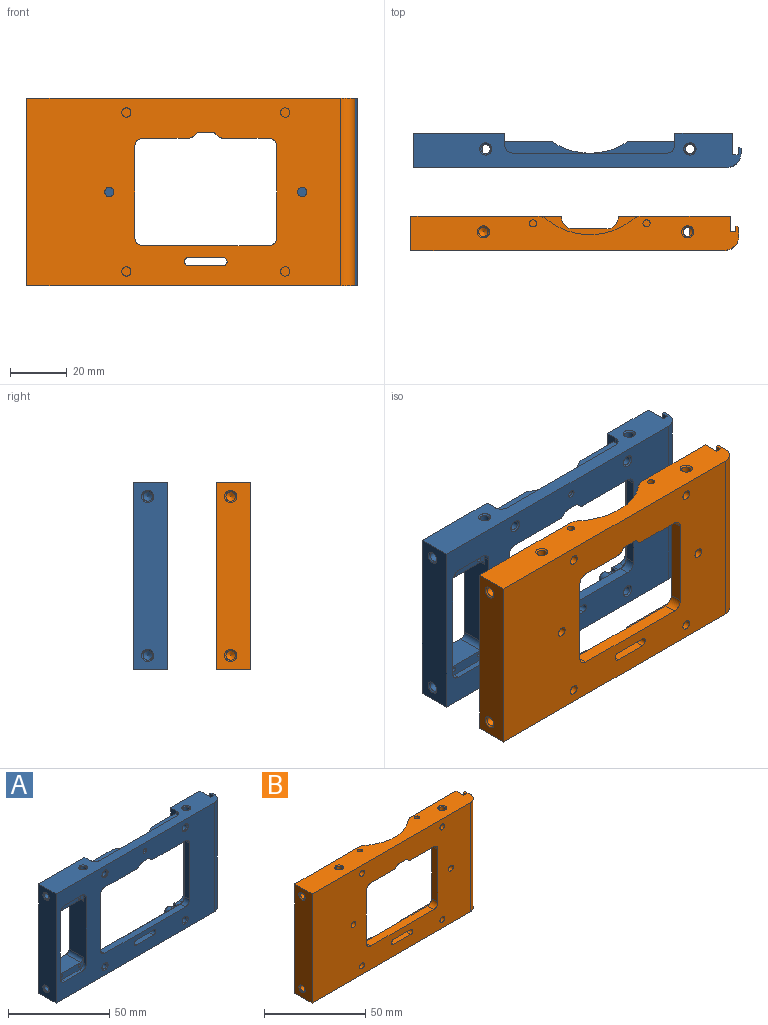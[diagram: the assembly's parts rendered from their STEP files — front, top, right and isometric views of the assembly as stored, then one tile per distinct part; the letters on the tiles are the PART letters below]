
ASSEMBLY  parts=2 mates=1
PART A: 193 faces, bbox 115.5x12x66 mm
  f0: plane 110.5x66mm, normal (0,-1,0), area 3867.2mm2, adj f15,f33,f34,f35,f36,f37,f38,f39
  f1: cylinder r=2mm len=10mm, axis (0,1,0), area 31.4mm2, adj f2,f31,f121,f173
  f2: plane 14.1x10mm, normal (0,0,-1), area 141mm2, adj f1,f3,f31,f173
  f3: cylinder r=2mm len=10mm, axis (0,1,0), area 31.4mm2, adj f2,f31,f122,f173
  f4: cylinder r=2mm len=10mm, axis (0,1,0), area 31.4mm2, adj f5,f31,f122,f177
  f5: plane 14.1x10mm, normal (0,0,1), area 141mm2, adj f4,f6,f31,f177
  f6: cylinder r=2mm len=10mm, axis (0,1,0), area 31.4mm2, adj f5,f31,f121,f177
  f7: cylinder r=0.8mm len=10mm, axis (0,-1,0), area 50.3mm2, adj f31,f173
  f8: cylinder r=0.8mm len=10mm, axis (0,-1,0), area 50.3mm2, adj f31,f177
  f9: cylinder r=0.8mm len=10mm, axis (0,-1,0), area 50.3mm2, adj f31,f177
  f10: cylinder r=0.8mm len=10mm, axis (0,-1,0), area 50.3mm2, adj f31,f173
  f11: plane 4.5x4.26mm, normal (1,0,0), area 19.2mm2, adj f15,f21,f139,f148
  f12: plane 4.5x4.26mm, normal (-1,0,0), area 19.2mm2, adj f15,f21,f140,f149
  f13: cylinder r=3.5mm len=4.5mm, axis (0,-1,0), area 6.6mm2, adj f21,f113,f139,f147
  f14: cylinder r=3.5mm len=4.5mm, axis (0,-1,0), area 6.6mm2, adj f18,f21,f140,f150
  f15: plane 115.5x12mm, normal (0,0,-1), area 923.5mm2, adj f0,f11,f12,f21,f24,f31,f54,f56
  f16: cylinder r=1.65mm len=8.5mm, axis (0,1,0), area 88.1mm2, adj f123,f140
  f17: cylinder r=1.65mm len=8.5mm, axis (0,1,0), area 88.1mm2, adj f126,f139
  f18: cylinder r=5mm len=7.5mm, axis (0,-1,0), area 16mm2, adj f14,f21,f24,f90,f119,f140
  f19: cylinder r=2mm len=4.5mm, axis (0,-1,0), area 26.3mm2, adj f21,f140,f149,f150
  f20: cylinder r=2mm len=4.5mm, axis (0,-1,0), area 26.3mm2, adj f21,f139,f147,f148
  f21: plane 78x56.5mm, normal (0,1,0), area 1353.3mm2, adj f11,f12,f13,f14,f15,f18,f19,f20
  f22: plane 8.11x7.5mm, normal (0,0,-1), area 48mm2, adj f21,f24,f49,f94,f116,f128,f138
  f23: plane 8.11x7.5mm, normal (0,0,-1), area 52.5mm2, adj f21,f31,f69,f93,f117,f127,f135
  f24: plane 66x20.3mm, normal (0,1,0), area 508.5mm2, adj f15,f18,f22,f55,f59,f86,f87,f90
  f25: cylinder r=24mm len=26.53mm, axis (0,0,1), area 208.8mm2, adj f28,f29,f30,f57,f127,f128
  f26: cylinder r=1.65mm len=8.5mm, axis (0,1,0), area 88.1mm2, adj f125,f127
  f27: cylinder r=1.65mm len=8.5mm, axis (0,1,0), area 88.1mm2, adj f124,f128
  f28: plane 43.29x4.5mm, normal (0,0,-1), area 122.8mm2, adj f21,f25,f127,f128,f136,f137
  f29: plane 30x4mm, normal (0,0,1), area 82.1mm2, adj f25,f114,f115,f116,f128
  f30: plane 30x4mm, normal (0,0,1), area 82.1mm2, adj f25,f114,f117,f118,f127
  f31: plane 66x32.2mm, normal (0,1,0), area 956.1mm2, adj f1,f2,f3,f4,f5,f6,f7,f8
  f32: plane 7.5x3.18mm, normal (0,0,1), area 21.8mm2, adj f21,f31,f64,f91,f113
  f33: plane 56.05x3.5mm, normal (0,0,1), area 196.2mm2, adj f0,f46,f47,f105
  f34: cylinder r=3mm len=3.5mm, axis (0,1,0), area 16.5mm2, adj f0,f35,f48,f111
  f35: plane 22.53x3.5mm, normal (0,0,-1), area 78.8mm2, adj f0,f34,f36,f112
  f36: cylinder r=1.45mm len=3.5mm, axis (0,1,0), area 3.5mm2, adj f0,f35,f37,f110
  f37: plane 3.5x1.59mm, normal (0.64,0,-0.77), area 7.3mm2, adj f0,f36,f38,f108
  f38: cylinder r=1.53mm len=3.5mm, axis (0,1,0), area 3.7mm2, adj f0,f37,f39,f106
  f39: plane 4x3.5mm, normal (0,0,-1), area 14mm2, adj f0,f38,f40,f104
  f40: cylinder r=1.53mm len=3.5mm, axis (0,1,0), area 3.7mm2, adj f0,f39,f41,f102
  f41: plane 3.5x1.59mm, normal (-0.64,0,-0.77), area 7.3mm2, adj f0,f40,f42,f100
  f42: cylinder r=1.45mm len=3.5mm, axis (0,1,0), area 3.5mm2, adj f0,f41,f43,f98
  f43: plane 22.53x3.5mm, normal (0,0,-1), area 78.8mm2, adj f0,f42,f44,f97
  f44: cylinder r=3mm len=3.5mm, axis (0,1,0), area 16.5mm2, adj f0,f43,f45,f99
  f45: plane 34.05x3.5mm, normal (-1,0,0), area 119.2mm2, adj f0,f44,f46,f101
  f46: cylinder r=3mm len=3.5mm, axis (0,1,0), area 16.5mm2, adj f0,f33,f45,f103
  f47: cylinder r=3mm len=3.5mm, axis (0,1,0), area 16.5mm2, adj f0,f33,f48,f107
  f48: plane 34.05x3.5mm, normal (1,0,0), area 119.2mm2, adj f0,f34,f47,f109
  f49: cylinder r=1.65mm len=9.15mm, axis (0,0,1), area 93.6mm2, adj f22,f71,f94
  f50: cylinder r=1.5mm len=4.5mm, axis (0,1,0), area 21.2mm2, adj f0,f21,f51,f53
  f51: plane 12x4.5mm, normal (0,0,-1), area 54mm2, adj f0,f21,f50,f52
  f52: cylinder r=1.5mm len=4.5mm, axis (0,1,0), area 21.2mm2, adj f0,f21,f51,f53
  f53: plane 12x4.5mm, normal (0,0,1), area 54mm2, adj f0,f21,f50,f52
  f54: plane 66x1.5mm, normal (1,0,0), area 99mm2, adj f15,f55,f58,f63
  f55: plane 115.5x12mm, normal (0,0,1), area 915.3mm2, adj f0,f24,f31,f54,f56,f58,f59,f60
  f56: plane 66x12mm, normal (-1,0,0), area 763mm2, adj f0,f15,f31,f55,f76,f77
  f57: cylinder r=0.8mm len=4.5mm, axis (0,1,0), area 22.6mm2, adj f25,f169
  f58: cylinder r=5mm len=66mm, axis (0,0,-1), area 518.4mm2, adj f0,f15,f54,f55
  f59: plane 66x7.5mm, normal (1,0,0), area 495mm2, adj f15,f24,f55,f60
  f60: plane 66x2mm, normal (0,1,0), area 132mm2, adj f15,f55,f59,f61
  f61: plane 66x2.5mm, normal (-1,0,0), area 165mm2, adj f15,f55,f60,f62
  f62: plane 66x0.5mm, normal (0,1,0), area 33mm2, adj f15,f55,f61,f63
  f63: plane 66x0.5mm, normal (0.71,0.71,0), area 46.7mm2, adj f15,f54,f55,f62
  f64: cylinder r=1.65mm len=7.64mm, axis (0,0,-1), area 70.8mm2, adj f32,f67,f91
  f65: cylinder r=1.65mm len=6.65mm, axis (0,0,-1), area 67.7mm2, adj f66,f90,f96
  f66: cone r=1.65mm half-angle=45deg, axis (0,0,-1), area 8.4mm2, adj f15,f65
  f67: cone r=1.65mm half-angle=45deg, axis (0,0,-1), area 8.4mm2, adj f15,f64
  f68: cone r=0mm half-angle=59deg, axis (0,0,1), area 0.9mm2, adj f69,f93
  f69: cylinder r=1.65mm len=9.5mm, axis (0,0,1), area 95.5mm2, adj f23,f68,f70,f93
  f70: cone r=1.65mm half-angle=45deg, axis (0,0,1), area 8.4mm2, adj f55,f69
  f71: cone r=1.65mm half-angle=45deg, axis (0,0,1), area 8.4mm2, adj f49,f55
  f72: cone r=0mm half-angle=59deg, axis (-1,0,0), area 10mm2, adj f73
  f73: cylinder r=1.65mm len=11.6mm, axis (-1,0,0), area 120.3mm2, adj f72,f77
  f74: cone r=0mm half-angle=59deg, axis (-1,0,0), area 10mm2, adj f75
  f75: cylinder r=1.65mm len=11.6mm, axis (-1,0,0), area 120.3mm2, adj f74,f76
  f76: cone r=1.65mm half-angle=45deg, axis (-1,0,0), area 8.4mm2, adj f56,f75
  f77: cone r=1.65mm half-angle=45deg, axis (-1,0,0), area 8.4mm2, adj f56,f73
  f78: cone r=0mm half-angle=59deg, axis (0,1,0), area 5.7mm2, adj f79
  f79: cylinder r=1.25mm len=8mm, axis (0,1,0), area 62.8mm2, adj f78,f89
  f80: cone r=0mm half-angle=59deg, axis (0,1,0), area 5.7mm2, adj f81
  f81: cylinder r=1.25mm len=8mm, axis (0,1,0), area 62.8mm2, adj f80,f88
  f82: cone r=0mm half-angle=59deg, axis (0,1,0), area 5.7mm2, adj f83
  f83: cylinder r=1.25mm len=8mm, axis (0,1,0), area 62.8mm2, adj f82,f87
  f84: cone r=0mm half-angle=59deg, axis (0,1,0), area 5.7mm2, adj f85
  f85: cylinder r=1.25mm len=8mm, axis (0,1,0), area 62.8mm2, adj f84,f86
  f86: cone r=1.25mm half-angle=45deg, axis (0,1,0), area 6.7mm2, adj f24,f85
  f87: cone r=1.25mm half-angle=45deg, axis (0,1,0), area 6.7mm2, adj f24,f83
  f88: cone r=1.25mm half-angle=45deg, axis (0,1,0), area 6.7mm2, adj f31,f81
  f89: cone r=1.25mm half-angle=45deg, axis (0,1,0), area 6.7mm2, adj f31,f79
  f90: plane 7.5x3.18mm, normal (0,0,1), area 17.3mm2, adj f18,f21,f24,f65,f96
  f91: cylinder r=3mm len=7.5mm, axis (0,1,0), area 28.1mm2, adj f21,f31,f32,f64,f92
  f92: plane 43.5x7.5mm, normal (1,0,0), area 326.2mm2, adj f21,f31,f91,f93
  f93: cylinder r=3mm len=7.5mm, axis (0,1,0), area 29.1mm2, adj f21,f23,f31,f68,f69,f92
  f94: cylinder r=3mm len=7.5mm, axis (0,1,0), area 33.3mm2, adj f21,f22,f24,f49,f95
  f95: plane 43.5x7.5mm, normal (-1,0,0), area 326.2mm2, adj f21,f24,f94,f96
  f96: cylinder r=3mm len=7.5mm, axis (0,1,0), area 33.3mm2, adj f21,f24,f65,f90,f95
  f97: plane 22.53x1mm, normal (0,0.71,-0.71), area 31.9mm2, adj f21,f43,f98,f99
  f98: cone r=0.45mm half-angle=45deg, axis (0,-1,0), area 0.9mm2, adj f21,f42,f97,f100
  f99: cone r=3mm half-angle=45deg, axis (0,1,0), area 7.8mm2, adj f21,f44,f97,f101
  f100: plane 2.23x2.1mm, normal (-0.45,0.71,-0.54), area 2.9mm2, adj f21,f41,f98,f102
  f101: plane 34.05x1mm, normal (-0.71,0.71,0), area 48.2mm2, adj f21,f45,f99,f103
  f102: cone r=1.53mm half-angle=45deg, axis (0,1,0), area 2mm2, adj f21,f40,f100,f104
  f103: cone r=3mm half-angle=45deg, axis (0,1,0), area 7.8mm2, adj f21,f46,f101,f105
  f104: plane 4x1mm, normal (0,0.71,-0.71), area 5.7mm2, adj f21,f39,f102,f106
  f105: plane 56.05x1mm, normal (0,0.71,0.71), area 79.3mm2, adj f21,f33,f103,f107
  f106: cone r=2.52mm half-angle=45deg, axis (0,1,0), area 2mm2, adj f21,f38,f104,f108
  f107: cone r=3mm half-angle=45deg, axis (0,1,0), area 7.8mm2, adj f21,f47,f105,f109
  f108: plane 2.23x2.1mm, normal (0.45,0.71,-0.54), area 2.9mm2, adj f21,f37,f106,f110
  f109: plane 34.05x1mm, normal (0.71,0.71,0), area 48.2mm2, adj f21,f48,f107,f111
  f110: cone r=1.45mm half-angle=45deg, axis (0,-1,0), area 0.9mm2, adj f21,f36,f108,f112
  f111: cone r=3mm half-angle=45deg, axis (0,1,0), area 7.8mm2, adj f21,f34,f109,f112
  f112: plane 22.53x1mm, normal (0,0.71,-0.71), area 31.9mm2, adj f21,f35,f110,f111
  f113: cylinder r=5mm len=7.5mm, axis (0,-1,0), area 16mm2, adj f13,f21,f31,f32,f120,f139
  f114: plane 54x2mm, normal (0,1,0), area 108mm2, adj f29,f30,f55,f115,f118
  f115: cylinder r=3mm len=3mm, axis (0,0,1), area 9.4mm2, adj f29,f55,f114,f116
  f116: plane 9.5x4mm, normal (-1,0,0), area 30.5mm2, adj f22,f24,f29,f55,f115,f128
  f117: plane 9.5x4mm, normal (1,0,0), area 30.5mm2, adj f23,f30,f31,f55,f118,f127
  f118: cylinder r=3mm len=3mm, axis (0,0,1), area 9.4mm2, adj f30,f55,f114,f117
  f119: plane 7.07x3mm, normal (-1,0,0), area 21.2mm2, adj f15,f18,f24,f140
  f120: plane 7.07x3mm, normal (1,0,0), area 21.2mm2, adj f15,f31,f113,f139
  f121: plane 40.1x12mm, normal (1,0,0), area 421.2mm2, adj f0,f1,f6,f31,f170,f173,f174,f177
  f122: plane 40.1x12mm, normal (-1,0,0), area 421.2mm2, adj f0,f3,f4,f31,f171,f173,f176,f177
  f123: cone r=1.65mm half-angle=45deg, axis (0,-1,0), area 8.4mm2, adj f0,f16
  f124: cone r=2.15mm half-angle=45deg, axis (0,-1,0), area 8.4mm2, adj f0,f27
  f125: cone r=1.65mm half-angle=45deg, axis (0,-1,0), area 8.4mm2, adj f0,f26
  f126: cone r=2.15mm half-angle=45deg, axis (0,-1,0), area 8.4mm2, adj f0,f17
  f127: plane 16.73x8.24mm, normal (0,1,0), area 114mm2, adj f23,f25,f26,f28,f30,f117,f132,f133
  f128: plane 16.73x8.24mm, normal (0,1,0), area 114mm2, adj f22,f25,f27,f28,f29,f116,f130,f134
  f129: cone r=0mm half-angle=59deg, axis (0,1,0), area 5.7mm2, adj f130
  f130: cylinder r=1.25mm len=5.5mm, axis (0,1,0), area 43.2mm2, adj f128,f129
  f131: cone r=0mm half-angle=59deg, axis (0,1,0), area 5.7mm2, adj f132
  f132: cylinder r=1.25mm len=5.5mm, axis (0,1,0), area 43.2mm2, adj f127,f131
  f133: cylinder r=2mm len=4.5mm, axis (0,1,0), area 8.3mm2, adj f21,f127,f135,f136
  f134: cylinder r=2mm len=4.5mm, axis (0,1,0), area 8.3mm2, adj f21,f128,f137,f138
  f135: cylinder r=5mm len=4.5mm, axis (0,1,0), area 10.4mm2, adj f21,f23,f127,f133
  f136: cylinder r=5mm len=4.5mm, axis (0,1,0), area 10.4mm2, adj f21,f28,f127,f133
  f137: cylinder r=5mm len=4.5mm, axis (0,1,0), area 10.4mm2, adj f21,f28,f128,f134
  f138: cylinder r=5mm len=4.5mm, axis (0,1,0), area 10.4mm2, adj f21,f22,f128,f134
  f139: plane 10.24x9.24mm, normal (0,1,0), area 55.4mm2, adj f11,f13,f15,f17,f20,f113,f120,f145
  f140: plane 10.24x9.24mm, normal (0,1,0), area 55.4mm2, adj f12,f14,f15,f16,f18,f19,f119,f146
  f141: cone r=0mm half-angle=59deg, axis (0,1,0), area 5.7mm2, adj f142
  f142: cylinder r=1.25mm len=5mm, axis (0,1,0), area 39.3mm2, adj f141,f145
  f143: cone r=0mm half-angle=59deg, axis (0,1,0), area 5.7mm2, adj f144
  f144: cylinder r=1.25mm len=5mm, axis (0,1,0), area 39.3mm2, adj f143,f146
  f145: cone r=1.25mm half-angle=45deg, axis (0,1,0), area 6.7mm2, adj f139,f142
  f146: cone r=1.25mm half-angle=45deg, axis (0,1,0), area 6.7mm2, adj f140,f144
  f147: cylinder r=5mm len=4.5mm, axis (0,1,0), area 12.8mm2, adj f13,f20,f21,f139
  f148: cylinder r=5mm len=4.5mm, axis (0,-1,0), area 13.6mm2, adj f11,f20,f21,f139
  f149: cylinder r=5mm len=4.5mm, axis (0,-1,0), area 13.6mm2, adj f12,f19,f21,f140
  f150: cylinder r=5mm len=4.5mm, axis (0,1,0), area 12.8mm2, adj f14,f19,f21,f140
  f151: cone r=0mm half-angle=59deg, axis (0,1,0), area 5.7mm2, adj f152
  f152: cylinder r=1.25mm len=2.5mm, axis (0,1,0), area 19.6mm2, adj f151,f168
  f153: cone r=0mm half-angle=59deg, axis (0,1,0), area 5.7mm2, adj f154
  f154: cylinder r=1.25mm len=2.5mm, axis (0,1,0), area 19.6mm2, adj f153,f163
  f155: cone r=0mm half-angle=59deg, axis (0,1,0), area 5.7mm2, adj f156
  f156: cylinder r=1.25mm len=2.5mm, axis (0,1,0), area 19.6mm2, adj f155,f164
  f157: cone r=0mm half-angle=59deg, axis (0,1,0), area 5.7mm2, adj f158
  f158: cylinder r=1.25mm len=2.5mm, axis (0,1,0), area 19.6mm2, adj f157,f165
  f159: cone r=0mm half-angle=59deg, axis (0,1,0), area 5.7mm2, adj f160
  f160: cylinder r=1.25mm len=2.5mm, axis (0,1,0), area 19.6mm2, adj f159,f166
  f161: cone r=0mm half-angle=59deg, axis (0,1,0), area 5.7mm2, adj f162
  f162: cylinder r=1.25mm len=2.5mm, axis (0,1,0), area 19.6mm2, adj f161,f167
  f163: cone r=1.25mm half-angle=45deg, axis (0,1,0), area 6.7mm2, adj f21,f154
  f164: cone r=1.25mm half-angle=45deg, axis (0,1,0), area 6.7mm2, adj f21,f156
  f165: cone r=1.25mm half-angle=45deg, axis (0,1,0), area 6.7mm2, adj f21,f158
  f166: cone r=1.25mm half-angle=45deg, axis (0,1,0), area 6.7mm2, adj f21,f160
  f167: cone r=1.25mm half-angle=45deg, axis (0,1,0), area 6.7mm2, adj f21,f162
  f168: cone r=1.25mm half-angle=45deg, axis (0,1,0), area 6.7mm2, adj f21,f152
  f169: cone r=0.8mm half-angle=45deg, axis (0,-1,0), area 4.7mm2, adj f0,f57
  f170: cylinder r=3mm len=3mm, axis (0,-1,0), area 9.4mm2, adj f0,f121,f172,f173
  f171: cylinder r=3mm len=3mm, axis (0,-1,0), area 9.4mm2, adj f0,f122,f172,f173
  f172: plane 12.1x2mm, normal (0,0,-1), area 24.2mm2, adj f0,f170,f171,f173
  f173: plane 18.1x6mm, normal (0,-1,0), area 66.2mm2, adj f1,f2,f3,f7,f10,f121,f122,f170
  f174: cylinder r=3mm len=3mm, axis (0,-1,0), area 9.4mm2, adj f0,f121,f175,f177
  f175: plane 12.1x2mm, normal (0,0,1), area 24.2mm2, adj f0,f174,f176,f177
  f176: cylinder r=3mm len=3mm, axis (0,-1,0), area 9.4mm2, adj f0,f122,f175,f177
  f177: plane 18.1x6mm, normal (0,-1,0), area 66.2mm2, adj f4,f5,f6,f8,f9,f121,f122,f174
  f178: plane 10x0.24mm, normal (0,0,-1), area 2.4mm2, adj f24,f179,f189,f190
  f179: cylinder r=1mm len=10mm, axis (0,1,0), area 15.7mm2, adj f24,f178,f180,f190
  f180: plane 10x5mm, normal (-1,0,0), area 50mm2, adj f24,f179,f190,f191
  f181: cylinder r=1.5mm len=10mm, axis (0,1,0), area 22.4mm2, adj f24,f182,f190,f191
  f182: plane 39.03x10mm, normal (-1,0,0), area 390.3mm2, adj f24,f181,f183,f190
  f183: cylinder r=1.5mm len=10mm, axis (0,1,0), area 22.4mm2, adj f24,f182,f190,f192
  f184: plane 10x5mm, normal (-1,0,0), area 50mm2, adj f24,f185,f190,f192
  f185: cylinder r=1mm len=10mm, axis (0,1,0), area 15.7mm2, adj f24,f184,f186,f190
  f186: plane 10x0.24mm, normal (0,0,1), area 2.4mm2, adj f24,f185,f187,f190
  f187: cylinder r=1mm len=10mm, axis (0,1,0), area 15.7mm2, adj f24,f186,f188,f190
  f188: plane 60x10mm, normal (1,0,0), area 600mm2, adj f24,f187,f189,f190
  f189: cylinder r=1mm len=10mm, axis (0,1,0), area 15.7mm2, adj f24,f178,f188,f190
  f190: plane 62x7.3mm, normal (0,1,0), area 356.5mm2, adj f178,f179,f180,f181,f182,f183,f184,f185
  f191: cylinder r=4mm len=10mm, axis (0,1,0), area 59.6mm2, adj f24,f180,f181,f190
  f192: cylinder r=4mm len=10mm, axis (0,1,0), area 59.6mm2, adj f24,f183,f184,f190
PART B: 99 faces, bbox 115.5x12x66 mm
  f0: plane 16.17x4.5mm, normal (0,0,-1), area 72.8mm2, adj f1,f8,f28,f92
  f1: plane 110.5x66mm, normal (0,-1,0), area 5290.3mm2, adj f0,f3,f4,f12,f13,f14,f16,f17
  f2: plane 66x53mm, normal (0,1,0), area 1897.5mm2, adj f3,f4,f9,f10,f21,f37,f44,f45
  f3: plane 70x12mm, normal (0,0,1), area 494mm2, adj f1,f2,f5,f6,f8,f12,f14,f50
  f4: plane 115.5x12mm, normal (0,0,1), area 1179.7mm2, adj f1,f2,f5,f11,f15,f31,f32,f33
  f5: plane 66x39.5mm, normal (0,1,0), area 1006.5mm2, adj f3,f4,f6,f7,f21,f32,f39,f40
  f6: plane 7.5x6mm, normal (-1,0,0), area 34.3mm2, adj f3,f5,f8,f41,f60,f61
  f7: plane 7.5x6mm, normal (-1,0,0), area 34.3mm2, adj f5,f8,f39,f48,f54,f55
  f8: plane 80x52mm, normal (0,1,0), area 2057.8mm2, adj f0,f3,f6,f7,f9,f10,f12,f13
  f9: plane 7.5x1mm, normal (0,0,1), area 7.5mm2, adj f2,f8,f44,f50
  f10: plane 7.5x1mm, normal (0,0,-1), area 7.5mm2, adj f2,f8,f45,f49
  f11: plane 66x0.5mm, normal (0,1,0), area 33mm2, adj f4,f21,f34,f35
  f12: cylinder r=1.5mm len=4.5mm, axis (0,1,0), area 21.2mm2, adj f1,f3,f8,f13
  f13: plane 12x4.5mm, normal (0,0,-1), area 54mm2, adj f1,f8,f12,f14
  f14: cylinder r=1.5mm len=4.5mm, axis (0,1,0), area 21.2mm2, adj f1,f3,f8,f13
  f15: plane 66x3mm, normal (1,0,0), area 198mm2, adj f4,f21,f31,f35
  f16: plane 44x4.5mm, normal (0,0,1), area 198mm2, adj f1,f8,f27,f30
  f17: plane 32x4.5mm, normal (1,0,0), area 144mm2, adj f1,f8,f27,f28
  f18: plane 16.17x4.5mm, normal (0,0,-1), area 72.8mm2, adj f1,f8,f29,f98
  f19: cylinder r=1.65mm len=4.5mm, axis (0,1,0), area 46.7mm2, adj f1,f8
  f20: cylinder r=1.65mm len=4.5mm, axis (0,1,0), area 46.7mm2, adj f1,f8
  f21: plane 115.5x12mm, normal (0,0,-1), area 1257.8mm2, adj f1,f2,f5,f11,f15,f31,f32,f33
  f22: plane 32x4.5mm, normal (-1,0,0), area 144mm2, adj f1,f8,f29,f30
  f23: cylinder r=1.65mm len=4.5mm, axis (0,1,0), area 46.7mm2, adj f1,f36
  f24: cylinder r=1.65mm len=4.5mm, axis (0,1,0), area 46.7mm2, adj f1,f42
  f25: cylinder r=1.65mm len=4.5mm, axis (0,1,0), area 46.7mm2, adj f1,f43
  f26: cylinder r=1.65mm len=4.5mm, axis (0,1,0), area 46.7mm2, adj f1,f38
  f27: cylinder r=3mm len=4.5mm, axis (0,-1,0), area 21.2mm2, adj f1,f8,f16,f17
  f28: cylinder r=3mm len=4.5mm, axis (0,1,0), area 21.2mm2, adj f0,f1,f8,f17
  f29: cylinder r=3mm len=4.5mm, axis (0,-1,0), area 21.2mm2, adj f1,f8,f18,f22
  f30: cylinder r=3mm len=4.5mm, axis (0,1,0), area 21.2mm2, adj f1,f8,f16,f22
  f31: cylinder r=5mm len=66mm, axis (0,0,-1), area 518.4mm2, adj f1,f4,f15,f21
  f32: plane 66x5.5mm, normal (1,0,0), area 363mm2, adj f4,f5,f21,f33
  f33: plane 66x2mm, normal (0,1,0), area 132mm2, adj f4,f21,f32,f34
  f34: plane 66x2mm, normal (-1,0,0), area 132mm2, adj f4,f11,f21,f33
  f35: plane 66x0.5mm, normal (0.71,0.71,0), area 46.7mm2, adj f4,f11,f15,f21
  f36: plane 3.3x3.3mm, normal (0,-1,0), area 8.6mm2, adj f23
  f37: plane 32x7.5mm, normal (1,0,0), area 240mm2, adj f2,f8,f44,f45
  f38: plane 3.3x3.3mm, normal (0,-1,0), area 8.6mm2, adj f26
  f39: plane 7.5x1mm, normal (0,0,-1), area 7.5mm2, adj f5,f7,f8,f47
  f40: plane 32x7.5mm, normal (-1,0,0), area 240mm2, adj f5,f8,f46,f47
  f41: plane 7.5x1mm, normal (0,0,1), area 7.5mm2, adj f5,f6,f8,f46
  f42: plane 3.3x3.3mm, normal (0,-1,0), area 8.6mm2, adj f24
  f43: plane 3.3x3.3mm, normal (0,-1,0), area 8.6mm2, adj f25
  f44: cylinder r=4mm len=7.5mm, axis (0,-1,0), area 47.1mm2, adj f2,f8,f9,f37
  f45: cylinder r=4mm len=7.5mm, axis (0,-1,0), area 47.1mm2, adj f2,f8,f10,f37
  f46: cylinder r=4mm len=7.5mm, axis (0,-1,0), area 47.1mm2, adj f5,f8,f40,f41
  f47: cylinder r=4mm len=7.5mm, axis (0,-1,0), area 47.1mm2, adj f5,f8,f39,f40
  f48: plane 70x7.5mm, normal (0,0,-1), area 361.8mm2, adj f2,f5,f7,f8,f49,f51,f52,f53
  f49: plane 7.5x6mm, normal (1,0,0), area 45mm2, adj f2,f8,f10,f48
  f50: plane 7.5x6mm, normal (1,0,0), area 45mm2, adj f2,f3,f8,f9
  f51: cylinder r=24mm len=30.28mm, axis (0,0,1), area 229.4mm2, adj f4,f48,f66,f67
  f52: cylinder r=1.25mm len=7mm, axis (0,0,1), area 55mm2, adj f4,f48
  f53: cylinder r=1.25mm len=7mm, axis (0,0,1), area 55mm2, adj f4,f48
  f54: cone r=0mm half-angle=59deg, axis (0,0,1), area 3.1mm2, adj f7,f55
  f55: cylinder r=1.65mm len=9.5mm, axis (0,0,1), area 79.9mm2, adj f7,f48,f54,f59
  f56: cone r=0mm half-angle=59deg, axis (0,0,1), area 10mm2, adj f57
  f57: cylinder r=1.65mm len=9.5mm, axis (0,0,1), area 98.5mm2, adj f56,f58
  f58: cone r=1.65mm half-angle=45deg, axis (0,0,1), area 8.4mm2, adj f4,f57
  f59: cone r=1.65mm half-angle=45deg, axis (0,0,1), area 8.4mm2, adj f4,f55
  f60: cone r=0mm half-angle=59deg, axis (0,0,-1), area 3.1mm2, adj f6,f61
  f61: cylinder r=1.65mm len=9.5mm, axis (0,0,-1), area 79.9mm2, adj f3,f6,f60,f65
  f62: cone r=0mm half-angle=59deg, axis (0,0,-1), area 10mm2, adj f63
  f63: cylinder r=1.65mm len=9.5mm, axis (0,0,-1), area 98.5mm2, adj f62,f64
  f64: cone r=1.65mm half-angle=45deg, axis (0,0,-1), area 8.4mm2, adj f21,f63
  f65: cone r=1.65mm half-angle=45deg, axis (0,0,-1), area 8.4mm2, adj f21,f61
  f66: cylinder r=5mm len=7mm, axis (0,0,1), area 23.9mm2, adj f2,f4,f48,f51
  f67: cylinder r=5mm len=7mm, axis (0,0,1), area 23.9mm2, adj f4,f5,f48,f51
  f68: plane 66x12mm, normal (-1,0,0), area 763mm2, adj f1,f2,f4,f21,f73,f74
  f69: cone r=0mm half-angle=59deg, axis (-1,0,0), area 10mm2, adj f70
  f70: cylinder r=1.65mm len=9.5mm, axis (-1,0,0), area 98.5mm2, adj f69,f74
  f71: cone r=0mm half-angle=59deg, axis (-1,0,0), area 10mm2, adj f72
  f72: cylinder r=1.65mm len=9.5mm, axis (-1,0,0), area 98.5mm2, adj f71,f73
  f73: cone r=1.65mm half-angle=45deg, axis (-1,0,0), area 8.4mm2, adj f68,f72
  f74: cone r=1.65mm half-angle=45deg, axis (-1,0,0), area 8.4mm2, adj f68,f70
  f75: cone r=0mm half-angle=59deg, axis (0,1,0), area 19.4mm2, adj f76
  f76: cylinder r=2.3mm len=7.5mm, axis (0,1,0), area 108.4mm2, adj f75,f86
  f77: cone r=0mm half-angle=59deg, axis (0,1,0), area 19.4mm2, adj f78
  f78: cylinder r=2.3mm len=7.5mm, axis (0,1,0), area 108.4mm2, adj f77,f85
  f79: cone r=0mm half-angle=59deg, axis (0,1,0), area 19.4mm2, adj f80
  f80: cylinder r=2.3mm len=7.5mm, axis (0,1,0), area 108.4mm2, adj f79,f84
  f81: cone r=0mm half-angle=59deg, axis (0,1,0), area 19.4mm2, adj f82
  f82: cylinder r=2.3mm len=7.5mm, axis (0,1,0), area 108.4mm2, adj f81,f83
  f83: cone r=2.3mm half-angle=45deg, axis (0,1,0), area 11.3mm2, adj f5,f82
  f84: cone r=2.3mm half-angle=45deg, axis (0,1,0), area 11.3mm2, adj f5,f80
  f85: cone r=2.3mm half-angle=45deg, axis (0,1,0), area 11.3mm2, adj f2,f78
  f86: cone r=2.3mm half-angle=45deg, axis (0,1,0), area 11.3mm2, adj f2,f76
  f87: plane 7x0.3mm, normal (-1,0,0), area 2.1mm2, adj f3,f5,f21,f88
  f88: cylinder r=4mm len=7mm, axis (0,0,-1), area 44mm2, adj f3,f21,f87,f89
  f89: plane 12x7mm, normal (0,1,0), area 84mm2, adj f3,f21,f88,f90
  f90: cylinder r=4mm len=7mm, axis (0,0,-1), area 44mm2, adj f3,f21,f89,f91
  f91: plane 7x0.3mm, normal (1,0,0), area 2.1mm2, adj f2,f3,f21,f90
  f92: cylinder r=2mm len=4.5mm, axis (0,1,0), area 7.1mm2, adj f0,f1,f8,f93
  f93: plane 4.5x0.83mm, normal (0.71,0,-0.71), area 5.3mm2, adj f1,f8,f92,f94
  f94: cylinder r=2mm len=4.5mm, axis (0,1,0), area 7.1mm2, adj f1,f8,f93,f95
  f95: plane 4.5x4.34mm, normal (0,0,-1), area 19.5mm2, adj f1,f8,f94,f96
  f96: cylinder r=2mm len=4.5mm, axis (0,1,0), area 7.1mm2, adj f1,f8,f95,f97
  f97: plane 4.5x0.83mm, normal (-0.71,0,-0.71), area 5.3mm2, adj f1,f8,f96,f98
  f98: cylinder r=2mm len=4.5mm, axis (0,1,0), area 7.1mm2, adj f1,f8,f18,f97
PLACE A t=(13.14,30.89,-2.6)mm
PLACE B t=(13.14,-5.84,-2.6)mm
MATE planar B.f4 <-> A.f55  axis (0,0,1) through (6.14,-4.82,30.4)mm
